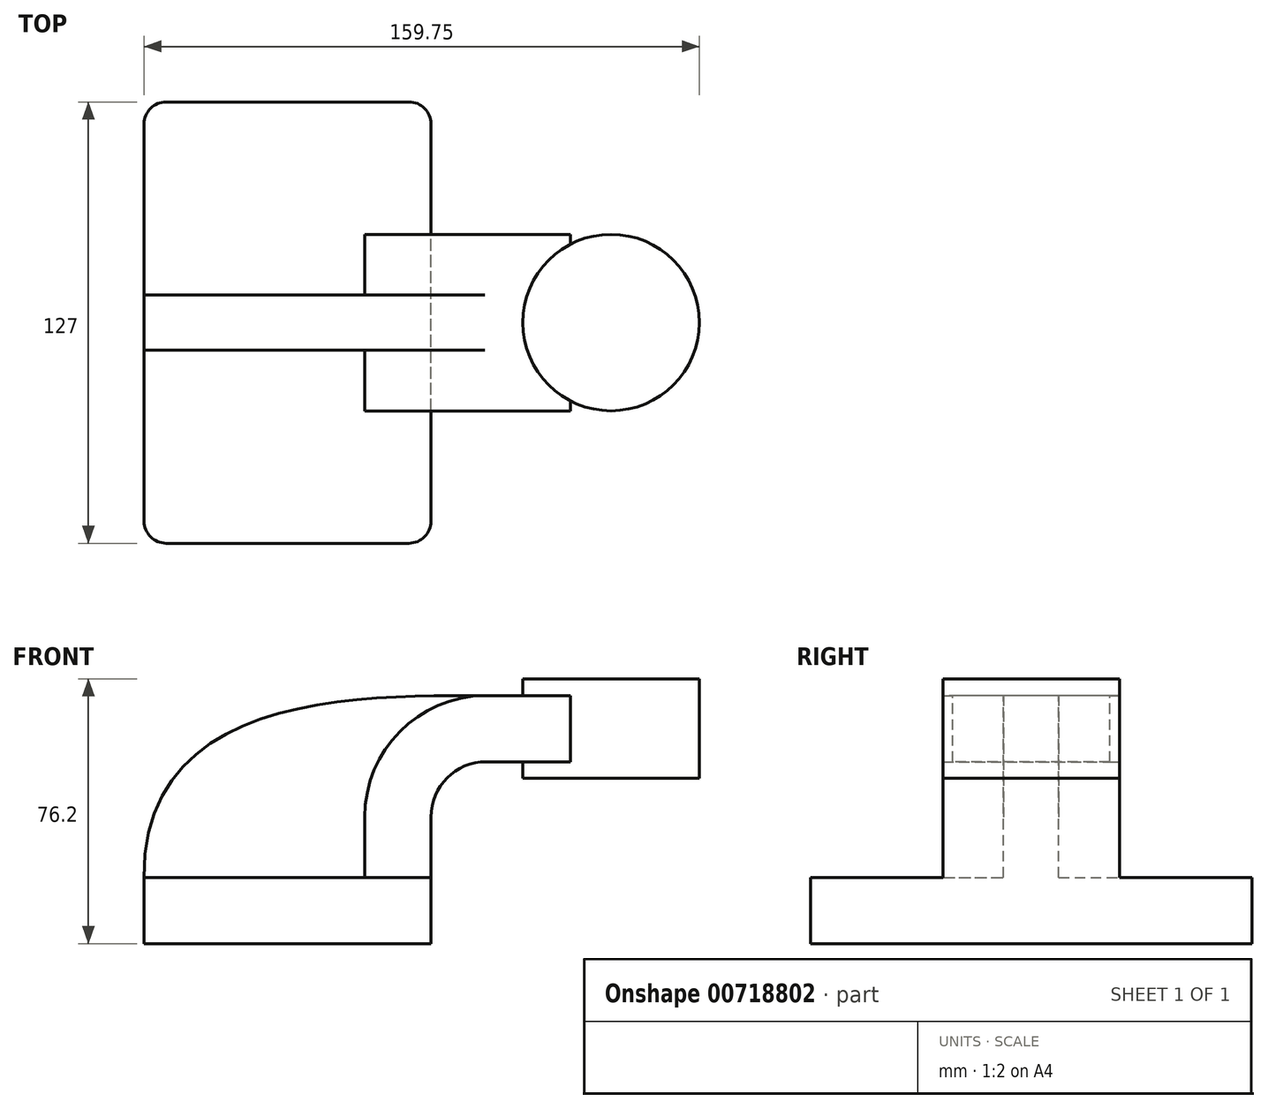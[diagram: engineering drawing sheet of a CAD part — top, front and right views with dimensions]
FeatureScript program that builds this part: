
annotation { "Feature Type Name" : "Feature", "Feature Type Description" : "" }
export const myFeature = defineFeature(function(context is Context, id is Id, definition is map)
    precondition{}
    {
        {
            var Q0;
            Q0=qCreatedBy(makeId("Front.planeOp"),FACE);
            var sketch = newSketch(context, id + "F0", { "sketchPlane" : qUnion([Q0])});
            skLineSegment(sketch, "E0", {"start": v(-26.74, 16.94) * mm, "end": v(-26.74, -2.11) * mm});
            skLineSegment(sketch, "E1", {"start": v(-26.74, -2.11) * mm, "end": v(55.8, -2.11) * mm});
            skLineSegment(sketch, "E2", {"start": v(55.8, -2.11) * mm, "end": v(55.8, 16.94) * mm});
            skLineSegment(sketch, "E3", {"start": v(55.8, 16.94) * mm, "end": v(-26.74, 16.94) * mm});
            skLineSegment(sketch, "E4", {"start": v(55.8, 16.94) * mm, "end": v(55.8, 34.34) * mm});
            skArc(sketch, "E5", {"start": v(55.8, 34.34) * mm, "mid": v(60.46, 45.56) * mm, "end": v(71.68, 50.21) * mm});
            skLineSegment(sketch, "E6", {"start": v(71.68, 50.21) * mm, "end": v(95.95, 50.21) * mm});
            skLineSegment(sketch, "E7.bottom", {"start": v(82.21, 74.09) * mm, "end": v(133.01, 74.09) * mm});
            skLineSegment(sketch, "E7.top", {"start": v(82.21, 45.51) * mm, "end": v(133.01, 45.51) * mm});
            skLineSegment(sketch, "E7.left", {"start": v(82.21, 74.09) * mm, "end": v(82.21, 45.51) * mm});
            skLineSegment(sketch, "E7.right", {"start": v(133.01, 74.09) * mm, "end": v(133.01, 45.51) * mm});
            skLineSegment(sketch, "E8.0", {"start": v(71.68, 69.26) * mm, "end": v(95.95, 69.26) * mm});
            skArc(sketch, "E8.1", {"start": v(36.76, 34.34) * mm, "mid": v(46.99, 59.03) * mm, "end": v(71.68, 69.26) * mm});
            skLineSegment(sketch, "E8.2", {"start": v(36.76, 16.94) * mm, "end": v(36.76, 34.34) * mm});
            skLineSegment(sketch, "E9", {"start": v(95.95, 69.26) * mm, "end": v(95.95, 50.21) * mm});
            skFitSpline(sketch, "E10", {"points": [v(-26.74, 16.94) * mm, v(71.68, 69.26) * mm], "startDerivative": vector(-1.3, 162.6) * mm, "endDerivative": vector(102.14, 0.54) * mm});
            skLineSegment(sketch, "E11", {"start": v(107.61, 74.09) * mm, "end": v(107.61, 45.51) * mm});
            skSolve(sketch);
        }
        {
            var Q0;
            {var subQ3=sQuery(id+"F0.wireOp",EDGE,"E0");Q0=makeQuery(id+"F0.imprint","IMPRINT",FACE,{"disambiguationData":[TD([[makeQuery(id+"F0.imprint","IMPRINT",EDGE,{"derivedFrom":subQ3}),1.0]])]});}
            extrude(context, id + "F1", {"entities" : qUnion([Q0]), "endBound" : BoundingType.SYMMETRIC, "depth" : 127 * mm, "offsetDistance" : 25.4 * mm});
        }
        {
            var Q0;
            {var subQ8=sQuery(id+"F0.wireOp",EDGE,"E4");Q0=makeQuery(id+"F0.imprint","IMPRINT",FACE,{"disambiguationData":[TD([[makeQuery(id+"F0.imprint","IMPRINT",EDGE,{"derivedFrom":subQ8}),1.0]])]});}
            var Q1;
            {var subQ0=sQuery(id+"F0.wireOp",EDGE,"E9");Q1=makeQuery(id+"F0.imprint","IMPRINT",FACE,{"disambiguationData":[TD([[makeQuery(id+"F0.imprint","IMPRINT",EDGE,{"derivedFrom":subQ0}),-1.0]])]});}
            extrude(context, id + "F2", {"entities" : qUnion([Q0, Q1]), "operationType" : NewBodyOperationType.ADD, "endBound" : BoundingType.SYMMETRIC, "depth" : 50.8 * mm, "offsetDistance" : 25.4 * mm});
        }
        {
            var Q0;
            {var subQ3=sQuery(id+"F0.wireOp",EDGE,"E8.2");Q0=makeQuery(id+"F0.imprint","IMPRINT",FACE,{"disambiguationData":[TD([[makeQuery(id+"F0.imprint","IMPRINT",EDGE,{"derivedFrom":subQ3}),1.0]])]});}
            extrude(context, id + "F3", {"entities" : qUnion([Q0]), "operationType" : NewBodyOperationType.ADD, "endBound" : BoundingType.SYMMETRIC, "depth" : 15.88 * mm, "offsetDistance" : 25.4 * mm});
        }
        {
            var Q0;
            {var subQ0=sQuery(id+"F0.wireOp",EDGE,"E7.right");Q0=makeQuery(id+"F0.imprint","IMPRINT",FACE,{"disambiguationData":[TD([[makeQuery(id+"F0.imprint","IMPRINT",EDGE,{"derivedFrom":subQ0}),-1.0]])]});}
            var Q1;
            Q1=sQuery(id+"F0.wireOp",EDGE,"E11");
            revolve(context, id + "F4", {"operationType" : NewBodyOperationType.ADD, "surfaceOperationType" : NewSurfaceOperationType.NEW, "entities" : qUnion([Q0]), "axis" : qUnion([Q1]), "revolveType" : RevolveType.FULL});
        }
        {
            var Q0;
            Q0=makeQuery(id+"F1.opExtrude","CAP_EDGE",EDGE,{"disambiguationData":[OSD([sQuery(id+"F0.wireOp",EDGE,"E0")])],"isStart":false});
            var Q1;
            Q1=makeQuery(id+"F1.opExtrude","CAP_EDGE",EDGE,{"disambiguationData":[OSD([sQuery(id+"F0.wireOp",EDGE,"E2")])],"isStart":false});
            var Q2;
            Q2=makeQuery(id+"F1.opExtrude","CAP_EDGE",EDGE,{"disambiguationData":[OSD([sQuery(id+"F0.wireOp",EDGE,"E2")])],"isStart":true});
            var Q3;
            Q3=makeQuery(id+"F1.opExtrude","CAP_EDGE",EDGE,{"disambiguationData":[OSD([sQuery(id+"F0.wireOp",EDGE,"E0")])],"isStart":true});
            fillet(context, id + "F5", {"entities" : qUnion([Q0, Q1, Q2, Q3]), "radius" : 6.35 * mm, "tangentPropagation" : true, "allowEdgeOverflow" : false});
        }
    });
